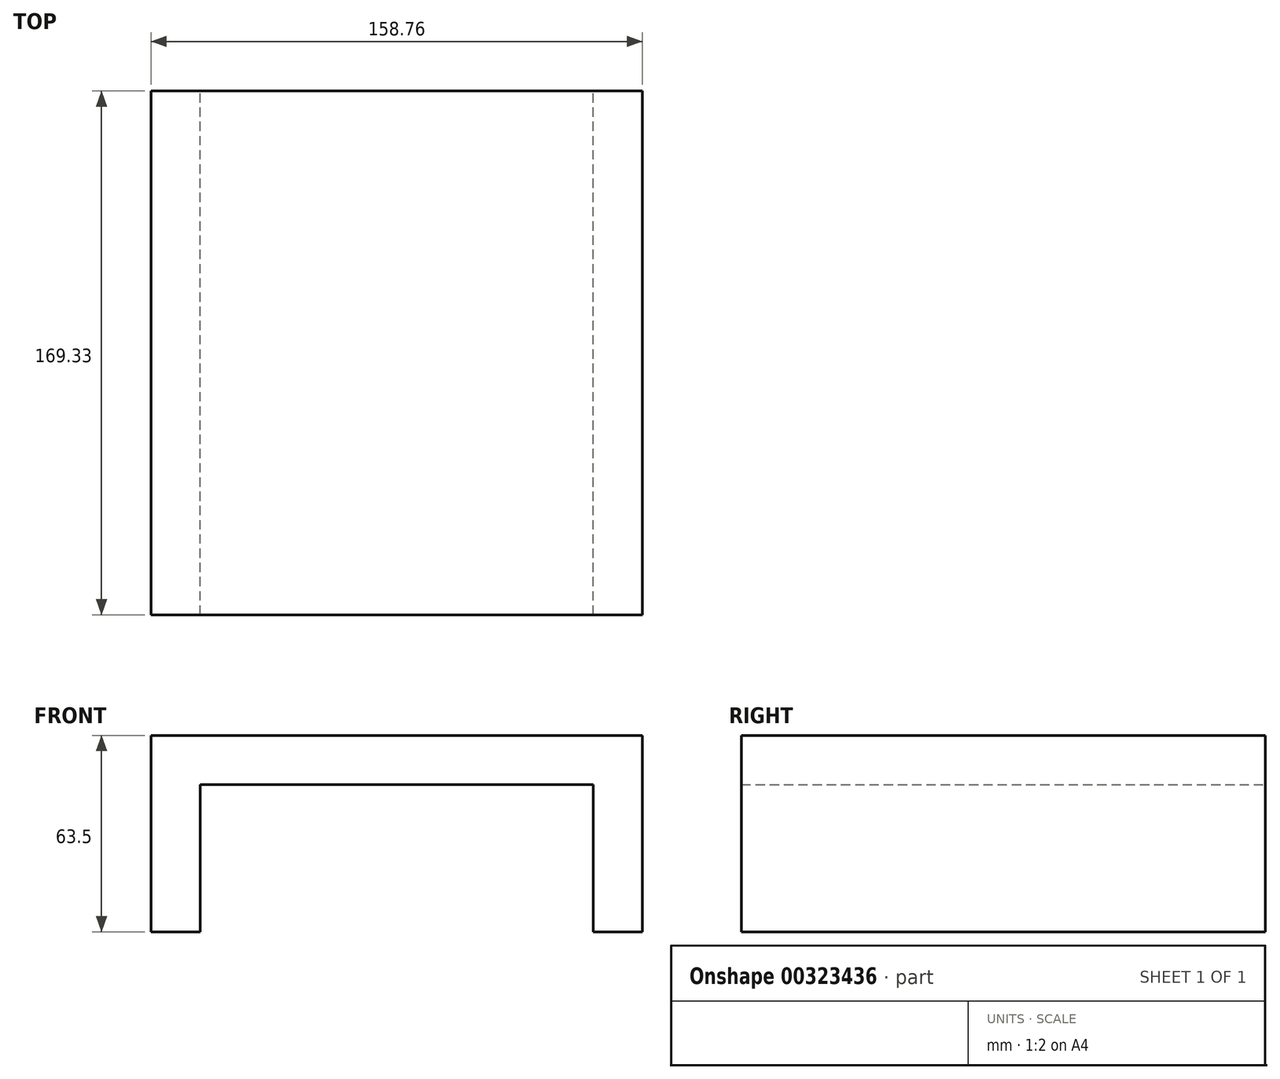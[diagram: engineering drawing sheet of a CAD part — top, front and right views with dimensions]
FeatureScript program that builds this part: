
annotation { "Feature Type Name" : "Feature", "Feature Type Description" : "" }
export const myFeature = defineFeature(function(context is Context, id is Id, definition is map)
    precondition{}
    {
        {
            var Q0;
            Q0=qCreatedBy(makeId("Front.planeOp"),FACE);
            var sketch = newSketch(context, id + "F0", { "sketchPlane" : qUnion([Q0])});
            skLineSegment(sketch, "E0", {"start": v(0, 0) * mm, "end": v(0, 47.63) * mm});
            skLineSegment(sketch, "E1", {"start": v(0, 47.63) * mm, "end": v(127, 47.63) * mm});
            skLineSegment(sketch, "E2", {"start": v(127, 47.63) * mm, "end": v(127, 0) * mm});
            skLineSegment(sketch, "E3.0", {"start": v(142.88, 63.5) * mm, "end": v(142.88, 0) * mm});
            skLineSegment(sketch, "E3.1", {"start": v(-15.87, 63.5) * mm, "end": v(142.88, 63.5) * mm});
            skLineSegment(sketch, "E3.2", {"start": v(-15.88, 0) * mm, "end": v(-15.88, 63.5) * mm});
            skLineSegment(sketch, "E4", {"start": v(0, 0) * mm, "end": v(-15.88, 0) * mm});
            skLineSegment(sketch, "E5", {"start": v(142.88, 0) * mm, "end": v(127, 0) * mm});
            skSolve(sketch);
        }
        {
            var Q0;
            Q0=makeQuery(id+"F0.imprint","IMPRINT",FACE,{"disambiguationData":[TD([[makeQuery(id+"F0.imprint","IMPRINT",EDGE,{"derivedFrom":sQuery(id+"F0.wireOp",EDGE,"E0")}),1.0]])]});
            extrude(context, id + "F1", {"entities" : qUnion([Q0]), "depth" : 169.33 * mm});
        }
    });
